# Revit family: Rohrschelle Trabant Inox, M10-M12, Gummi, V4A
name_source: partatom
category: HLS-Bauteile
revit_build: Autodesk Revit 2017 (Build: 20190507_1515(x64)
units: mm (PartAtom-declared; Revit-internal decimal feet)

## family parameters
Arbeitsebenenbasiert = Ja
Beim Laden mit Abzugskörper schneiden = Nein
Bemaßung runder Anschluss = Durchmesser verwenden
Gemeinsam genutzt = Ja
Immer vertikal = Nein
Raumberechnungspunkt = Nein
Teiletyp = Normal

## types (6) — shared parameters
A = 29 mm
Anschluss = M10/M12
Anschlußhöhe = 27 mm
Bauart = zweiteilig
Baustoffklasse = B2
Breite Material = 25 mm
DF1 = 17 mm
DF2 = 21 mm  [stored 0.0688976 ft]
DS = 5 mm  [stored 0.0164042 ft]
DVS = 5 mm  [stored 0.0164042 ft]
Dämmstärke = 5 mm  [stored 0.0164042 ft]
Fabrikat = MEFA
Farbe Schalldämmeinlage = schwarz
Firma = MEFA Befestigungs- und Montagesysteme GmbH
H1 = 2 mm  [stored 0.00656168 ft]
HGA = 22 mm  [stored 0.0721785 ft]
Kurztext1 = Rohrschelle Trabant Inox 25x2,5
MB = 25 mm  [stored 0.082021 ft]
MD = 3 mm  [stored 0.00984252 ft]
Material = Edelstahl
Material Schalldämmeinlage = TPE
Materialmaße = 25x2,5 mm
Mengeneinheit = St
Schalldämmeinlage = Gummi
Stärke Material = 3 mm  [stored 0.00984252 ft]
Verschluss = Rastverschluss
Verschluss-Schraube = M6
Vorgabe-Ansicht = 1219 mm
max. Temperaturbeständigkeit = 100 °C
max. zul. Last horizontal = 0.00 kN
max. zul. Last vertikal = 0.00 kN
zero-valued in all types: Nennweite DN Rohr, Rohraußendurchmesser

## per-type parameters (varying)
| type | AB | Achsabstand | Artikelnummer | B | D | D0 | Dmax | Dmin | EAN | Gewicht | Gewicht pro Bauteil | H | H2 | Kurztext2 | R | RM | Rohraußendurchmesser Zoll | S | max. Rohraußendurchmesser | min. Rohraußendurchmesser | vpe |
| Trabant Inox, M10/M12, Ø132-136, Gummi, V4A | 4 mm  [stored 0.0131234 ft] | 171 mm | 051003136 | 188 mm | 136 mm | 145 mm | 136 mm | 132 mm  [stored 0.433071 ft] | 4250928453969 | 0.35 kg | 0.35 kg | 172 mm | 6 mm  [stored 0.019685 ft] | 132 - 136 mm M10/M12 TPE | 73 mm | 77 mm  [stored 0.252625 ft] |  | 171 mm | 136 mm | 132 mm  [stored 0.433071 ft] | 25 St |
| Trabant Inox, M10/M12, Ø137-141, Gummi, V4A | 4 mm  [stored 0.0131234 ft] | 176 mm | 051003141 | 193 mm | 141 mm | 150 mm | 141 mm | 137 mm  [stored 0.449475 ft] | 4250928453976 | 0.36 kg | 0.36 kg | 177 mm | 6 mm  [stored 0.019685 ft] | 137 - 141 mm M10/M12 TPE | 75 mm | 80 mm | 5 Zoll | 176 mm | 141 mm | 137 mm  [stored 0.449475 ft] | 25 St |
| Trabant Inox, M10/M12, Ø159-163, Gummi, V4A | 4 mm  [stored 0.0131234 ft] | 198 mm | 051003163 | 215 mm | 163 mm | 172 mm | 163 mm | 159 mm  [stored 0.521654 ft] | 4250928453983 | 0.40 kg | 0.40 kg | 199 mm | 6 mm  [stored 0.019685 ft] | 159 - 163 mm M10/M12 TPE | 86 mm | 91 mm |  | 198 mm | 163 mm | 159 mm  [stored 0.521654 ft] | 25 St |
| Trabant Inox, M10/M12, Ø164-168, Gummi, V4A | 4 mm  [stored 0.0131234 ft] | 203 mm | 051003168 | 220 mm | 168 mm | 177 mm | 168 mm | 164 mm | 4250928453990 | 0.42 kg | 0.42 kg | 204 mm | 6 mm  [stored 0.019685 ft] | 164 - 168 mm M10/M12 TPE | 89 mm  [stored 0.291995 ft] | 93 mm  [stored 0.305118 ft] | 6 Zoll | 203 mm | 168 mm | 164 mm | 25 St |
| Trabant Inox, M10/M12, Ø 98-102, Gummi, V4A | 4 mm  [stored 0.0131234 ft] | 136 mm | 051003102 | 154 mm  [stored 0.505249 ft] | 102 mm | 111 mm | 102 mm | 98 mm  [stored 0.321522 ft] | 4250928453945 | 0.26 kg | 0.26 kg | 138 mm  [stored 0.452756 ft] | 6 mm  [stored 0.019685 ft] | 98 - 102 mm M10/M12 TPE | 56 mm | 60 mm |  | 137 mm  [stored 0.449475 ft] | 102 mm | 98 mm  [stored 0.321522 ft] | 50 St |
| Trabant Inox, M10/M12, Ø108-114, Gummi, V4A | 6 mm  [stored 0.019685 ft] | 148 mm | 051003114 | 166 mm | 114 mm  [stored 0.374016 ft] | 123 mm  [stored 0.403543 ft] | 114 mm  [stored 0.374016 ft] | 108 mm  [stored 0.354331 ft] | 4250928453952 | 0.29 kg | 0.29 kg | 150 mm | 7 mm  [stored 0.0229659 ft] | 108 - 114 mm M10/M12 TPE | 62 mm | 67 mm | 4 Zoll | 149 mm  [stored 0.488845 ft] | 114 mm  [stored 0.374016 ft] | 108 mm  [stored 0.354331 ft] | 50 St |

note: [stored X ft] marks values corroborated as IEEE doubles in the binary element streams (Revit-internal decimal feet)

## geometry (parser evidence)
native form markers: Sweep x3
no freeform markers — native parametric forms only
